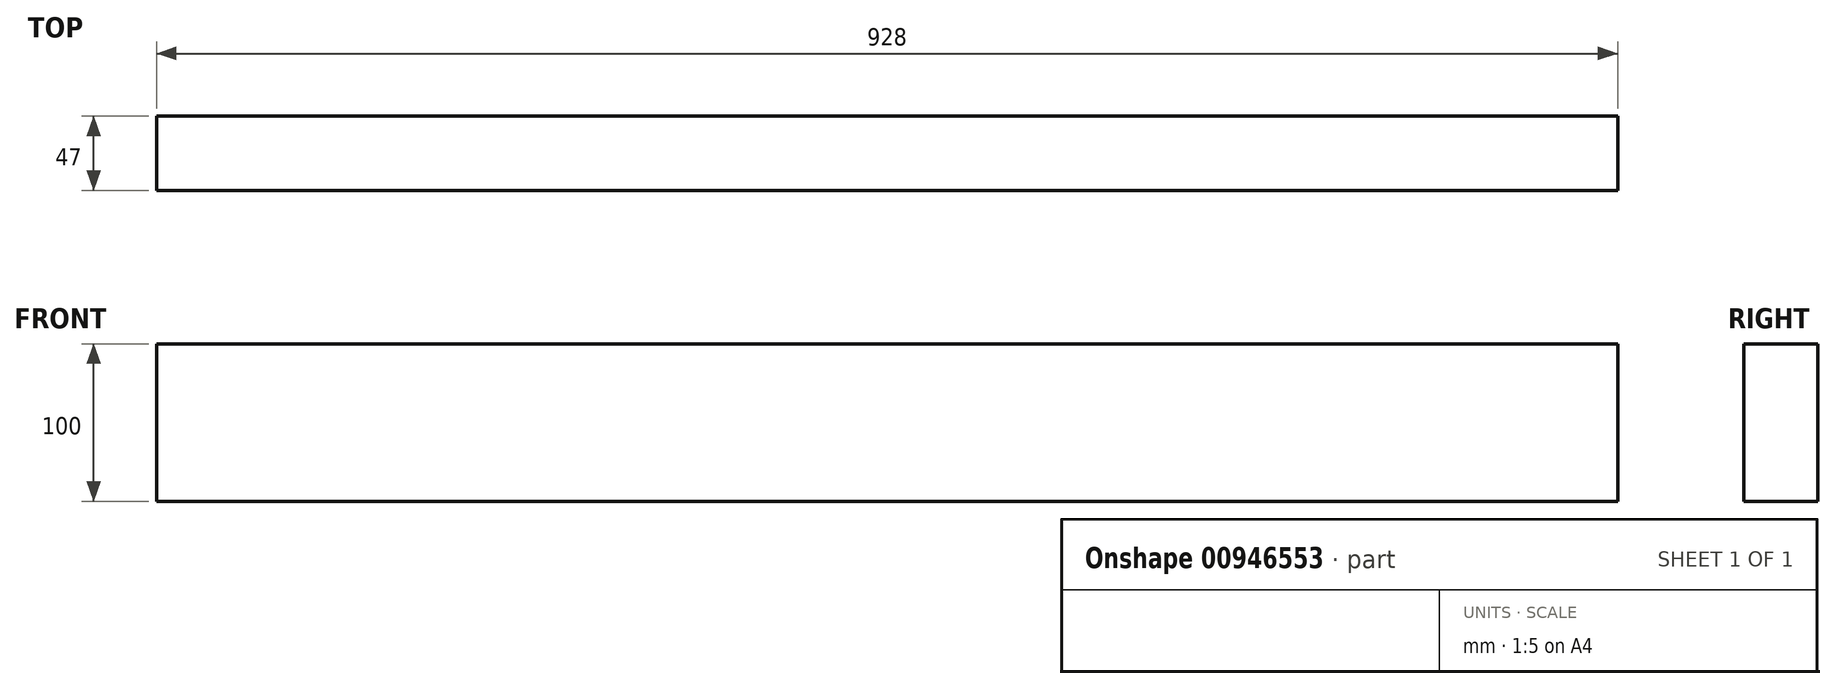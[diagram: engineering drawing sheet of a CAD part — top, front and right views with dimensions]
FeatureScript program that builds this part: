
annotation { "Feature Type Name" : "Feature", "Feature Type Description" : "" }
export const myFeature = defineFeature(function(context is Context, id is Id, definition is map)
    precondition{}
    {
        {
            var Q0;
            Q0=qCreatedBy(makeId("Right.planeOp"),FACE);
            var sketch = newSketch(context, id + "F0", { "sketchPlane" : qUnion([Q0])});
            skLineSegment(sketch, "E0.bottom", {"start": v(0, 0) * mm, "end": v(-47, 0) * mm});
            skLineSegment(sketch, "E0.top", {"start": v(0, 100) * mm, "end": v(-47, 100) * mm});
            skLineSegment(sketch, "E0.left", {"start": v(0, 0) * mm, "end": v(0, 100) * mm});
            skLineSegment(sketch, "E0.right", {"start": v(-47, 0) * mm, "end": v(-47, 100) * mm});
            skSolve(sketch);
        }
        {
            var Q0;
            Q0=qSketchRegion(id+"F0",true);
            extrude(context, id + "F1", {"entities" : qUnion([Q0]), "depth" : 928 * mm, "offsetDistance" : 25 * mm});
        }
    });
